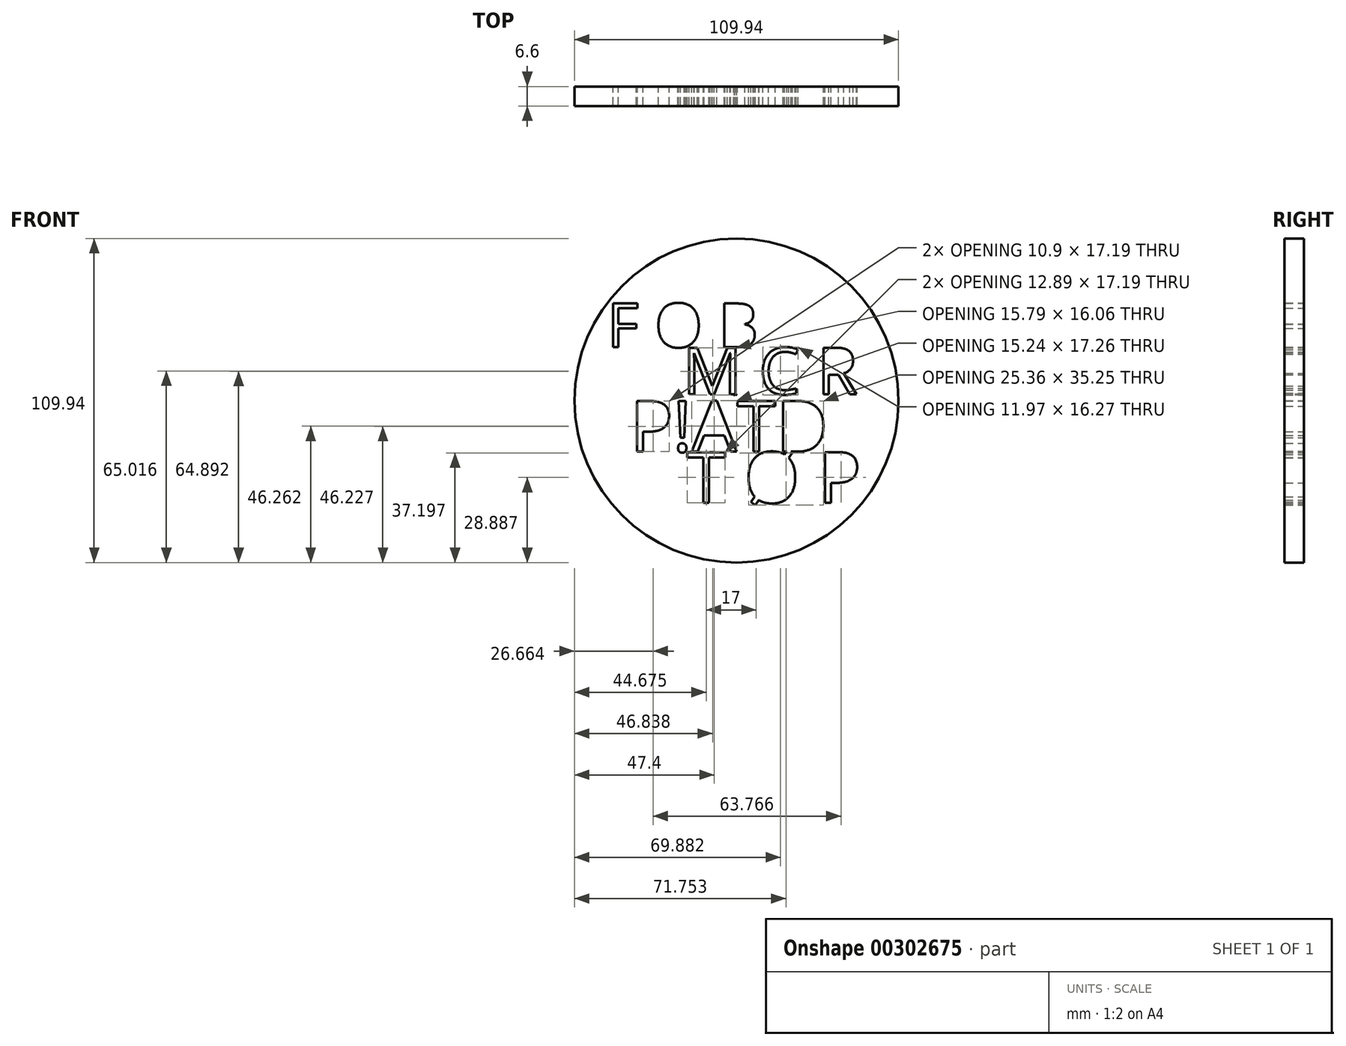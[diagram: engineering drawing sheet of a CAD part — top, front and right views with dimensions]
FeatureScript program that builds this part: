
annotation { "Feature Type Name" : "Feature", "Feature Type Description" : "" }
export const myFeature = defineFeature(function(context is Context, id is Id, definition is map)
    precondition{}
    {
        {
            var Q0;
            Q0=qCreatedBy(makeId("Front.planeOp"),FACE);
            var sketch = newSketch(context, id + "F0", { "sketchPlane" : qUnion([Q0])});
            skCircle(sketch, "E0", {"center": v(0, 0) * mm, "radius": 54.97 * mm});
            skText(sketch, "E1", { "text": "F O B", "fontName": "OpenSans-Regular.ttf"});
            skText(sketch, "E2", { "text": "M C R", "fontName": "OpenSans-Regular.ttf"});
            skText(sketch, "E3", { "text": "P!ATD", "fontName": "OpenSans-Regular.ttf"});
            skText(sketch, "E4", { "text": "P!ATD", "fontName": "OpenSans-Regular.ttf"});
            skText(sketch, "E5", { "text": "T Ø P", "fontName": "OpenSans-Regular.ttf"});
            const initialGuessF0  = {"E1": [-0.0439, 0.0181, 1, 0, 0.01498], "E2": [-0.0182, 0.00213, 1, 0, 0.01596], "E3": [-0.00095, 0.00189, 1, 0, 0.00025], "E4": [-0.03612, -0.01734, 1, 0, 0.01734], "E5": [-0.01695, -0.03468, 1, 0, 0.01734]};
            skSetInitialGuess(sketch, initialGuessF0);
            skSolve(sketch);
        }
        {
            var Q0;
            Q0 = qSketchRegion(id + "F0", true);
            extrude(context, id + "F1", {"entities" : qUnion([Q0]), "depth" : 6.6 * mm});
        }
    });
